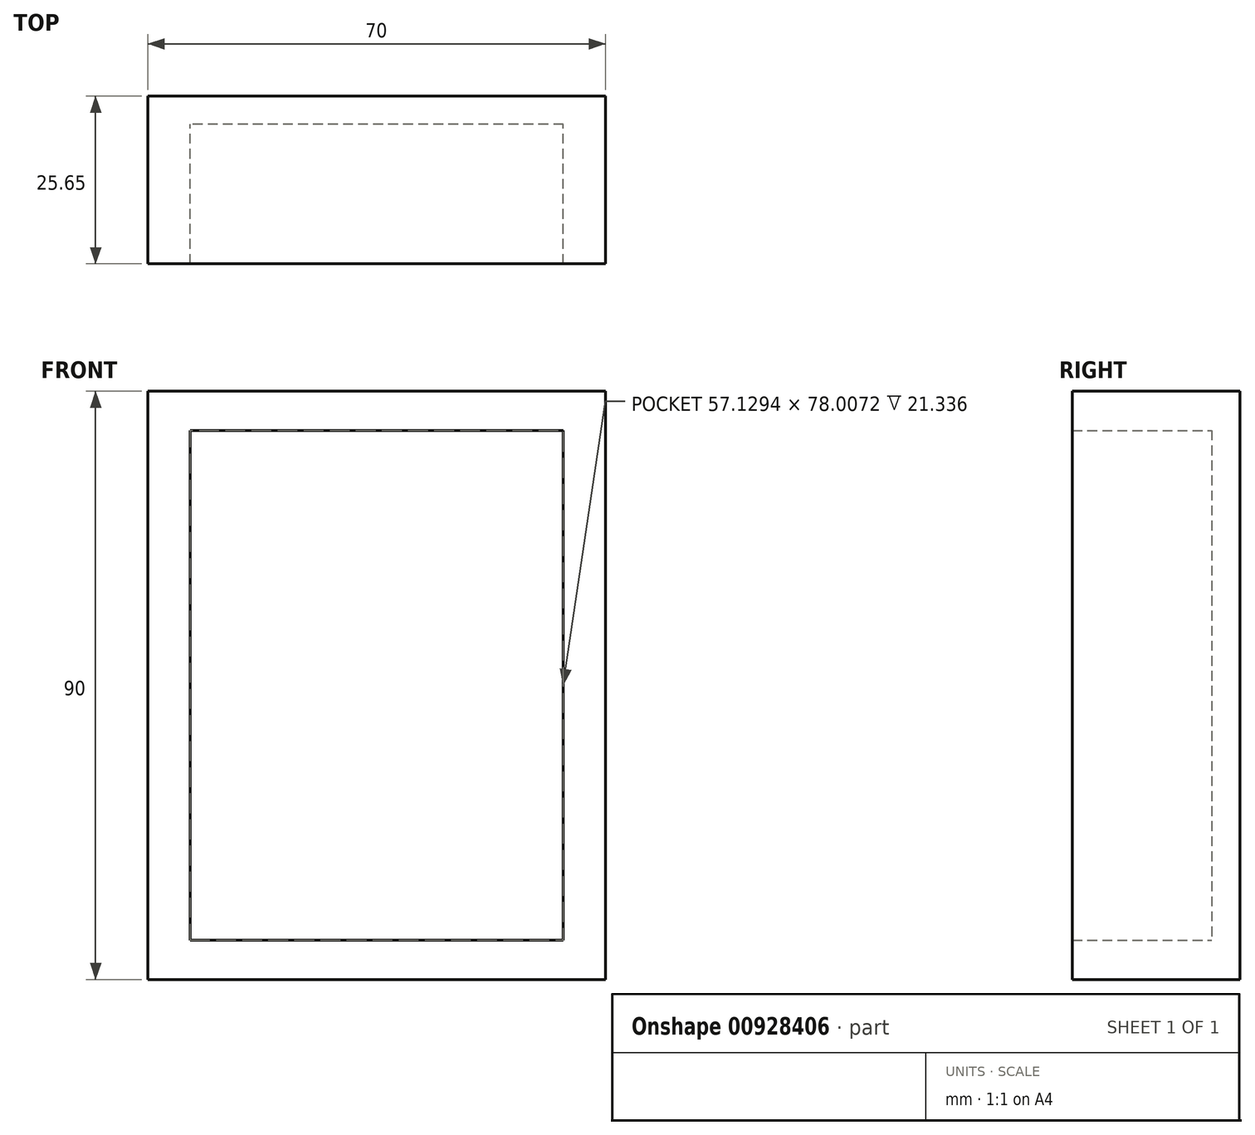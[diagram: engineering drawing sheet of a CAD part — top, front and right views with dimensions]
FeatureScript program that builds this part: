
annotation { "Feature Type Name" : "Feature", "Feature Type Description" : "" }
export const myFeature = defineFeature(function(context is Context, id is Id, definition is map)
    precondition{}
    {
        {
            var Q0;
            Q0=qCreatedBy(makeId("Front.planeOp"),FACE);
            var sketch = newSketch(context, id + "F0", { "sketchPlane" : qUnion([Q0])});
            skLineSegment(sketch, "E0.bottom", {"start": v(35, 45) * mm, "end": v(-35, 45) * mm});
            skLineSegment(sketch, "E0.top", {"start": v(35, -45) * mm, "end": v(-35, -45) * mm});
            skLineSegment(sketch, "E0.left", {"start": v(35, 45) * mm, "end": v(35, -45) * mm});
            skLineSegment(sketch, "E0.right", {"start": v(-35, 45) * mm, "end": v(-35, -45) * mm});
            skPoint(sketch, "E0.middle", {"position": v(0, 0) * mm});
            skLineSegment(sketch, "E1.bottom", {"start": v(28.56, 39) * mm, "end": v(-28.56, 39) * mm});
            skLineSegment(sketch, "E1.top", {"start": v(28.56, -39) * mm, "end": v(-28.56, -39) * mm});
            skLineSegment(sketch, "E1.left", {"start": v(28.56, 39) * mm, "end": v(28.56, -39) * mm});
            skLineSegment(sketch, "E1.right", {"start": v(-28.56, 39) * mm, "end": v(-28.56, -39) * mm});
            skSolve(sketch);
        }
        {
            var Q0;
            Q0 = qSketchRegion(id + "F0", true);
            extrude(context, id + "F1", {"entities" : qUnion([Q0]), "depth" : 25.65 * mm, "offsetDistance" : 25.4 * mm});
        }
        {
            var Q0;
            Q0=qCreatedBy(makeId("Front.planeOp"),FACE);
            var sketch = newSketch(context, id + "F2", { "sketchPlane" : qUnion([Q0])});
            skLineSegment(sketch, "E2.bottom", {"start": v(35, 45) * mm, "end": v(-35, 45) * mm});
            skLineSegment(sketch, "E2.top", {"start": v(35, -45) * mm, "end": v(-35, -45) * mm});
            skLineSegment(sketch, "E2.left", {"start": v(35, 45) * mm, "end": v(35, -45) * mm});
            skLineSegment(sketch, "E2.right", {"start": v(-35, 45) * mm, "end": v(-35, -45) * mm});
            skPoint(sketch, "E2.middle", {"position": v(0, 0) * mm});
            skSolve(sketch);
        }
        {
            var Q0;
            Q0 = qSketchRegion(id + "F2", true);
            extrude(context, id + "F3", {"entities" : qUnion([Q0]), "operationType" : NewBodyOperationType.ADD, "depth" : 4.32 * mm, "offsetDistance" : 25.4 * mm});
        }
    });
